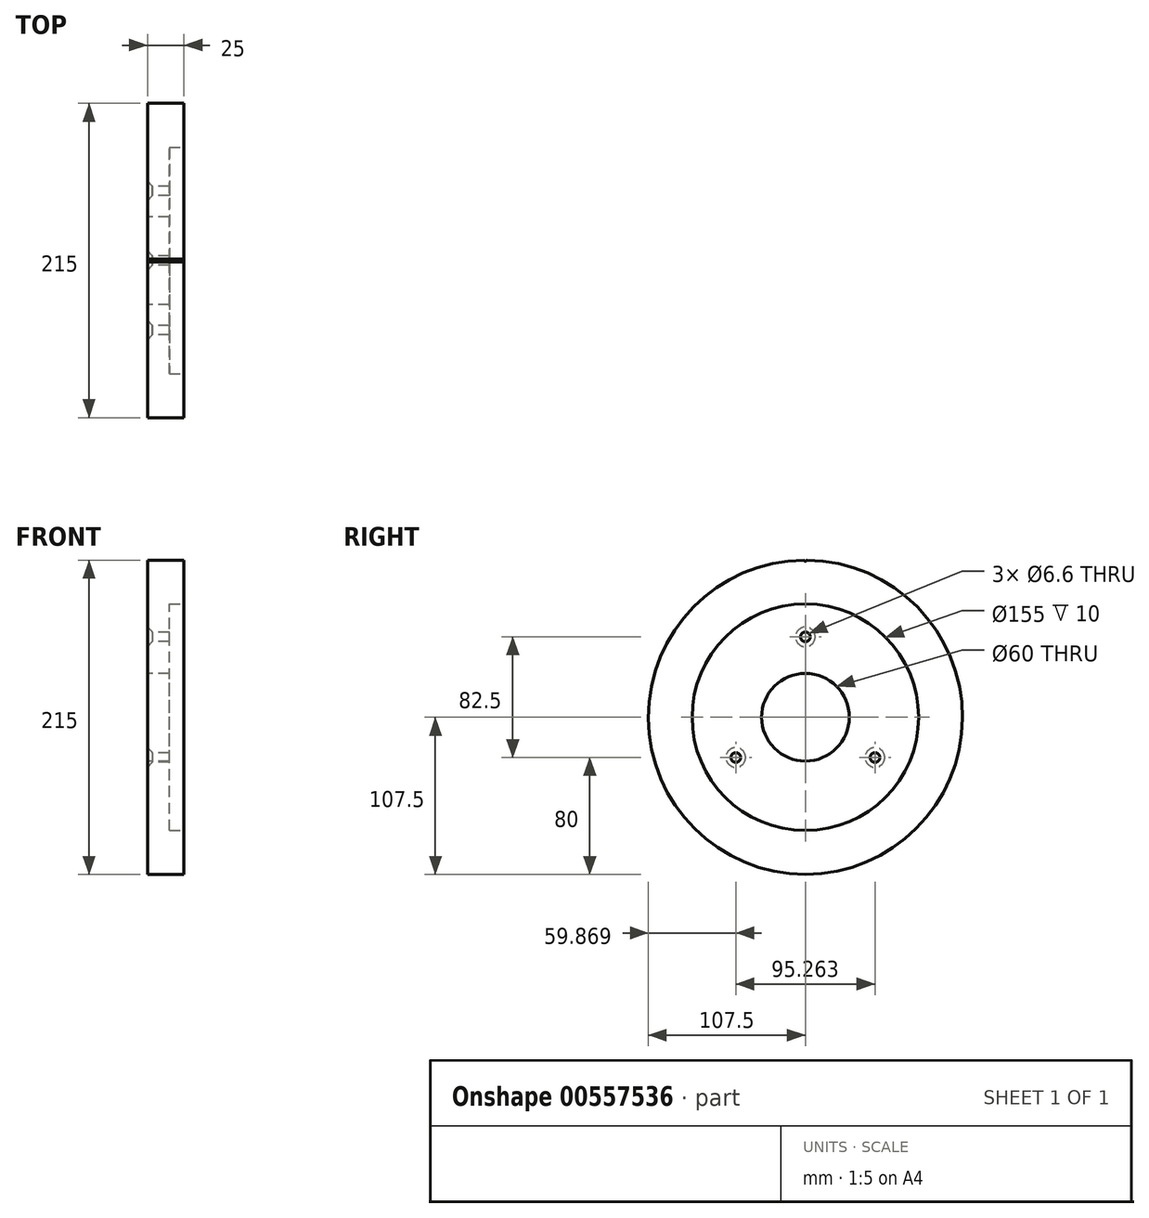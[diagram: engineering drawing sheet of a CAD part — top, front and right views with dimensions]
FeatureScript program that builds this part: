
annotation { "Feature Type Name" : "Feature", "Feature Type Description" : "" }
export const myFeature = defineFeature(function(context is Context, id is Id, definition is map)
    precondition{}
    {
        {
            var Q0;
            Q0=qCreatedBy(makeId("Right.planeOp"),FACE);
            var sketch = newSketch(context, id + "F0", { "sketchPlane" : qUnion([Q0])});
            skCircle(sketch, "E0", {"center": v(0, 0) * mm, "radius": 107.5 * mm});
            skSolve(sketch);
        }
        {
            var Q0;
            Q0 = qSketchRegion(id + "F0", true);
            extrude(context, id + "F1", {"entities" : qUnion([Q0]), "depth" : 25 * mm, "offsetDistance" : 25 * mm});
        }
        {
            var Q0;
            Q0=makeQuery(id+"F1.opExtrude","CAP_FACE",FACE,{"disambiguationData":[OSD([sQuery(id+"F0.wireOp",EDGE,"E0")])],"isStart":false});
            var sketch = newSketch(context, id + "F2", { "sketchPlane" : qUnion([Q0])});
            skCircle(sketch, "E1", {"center": v(0, 0) * mm, "radius": 77.5 * mm});
            skSolve(sketch);
        }
        {
            var Q0;
            Q0 = qSketchRegion(id + "F2", true);
            extrude(context, id + "F3", {"entities" : qUnion([Q0]), "operationType" : NewBodyOperationType.REMOVE, "oppositeDirection" : true, "depth" : 10 * mm, "offsetDistance" : 25 * mm});
        }
        {
            var Q0;
            Q0=makeQuery(id+"F1.opExtrude","CAP_FACE",FACE,{"disambiguationData":[OSD([sQuery(id+"F0.wireOp",EDGE,"E0")])],"isStart":true});
            var sketch = newSketch(context, id + "F4", { "sketchPlane" : qUnion([Q0])});
            skPoint(sketch, "E2", {"position": v(0, 55) * mm});
            skPoint(sketch, "E3.1.0", {"position": v(-47.63, -27.5) * mm});
            skPoint(sketch, "E3.2.0", {"position": v(47.63, -27.5) * mm});
            skPoint(sketch, "E3.center", {"position": v(0, 0) * mm});
            skSolve(sketch);
        }
        {
            var Q0;
            Q0=sQuery(id+"F4.wireOp",VERTEX,"E2");
            var Q1;
            Q1=sQuery(id+"F4.wireOp",VERTEX,"E3.2.0");
            var Q2;
            Q2=sQuery(id+"F4.wireOp",VERTEX,"E3.1.0");
            var Q3;
            Q3=makeQuery(id+"F1.opExtrude","SWEPT_BODY",BODY,{"disambiguationData":[OSD([sQuery(id+"F0.wireOp",EDGE,"E0")])]});
            hole(context, id + "F5", {"style" : HoleStyle.C_SINK, "endStyle" : HoleEndStyle.THROUGH, "standardTappedOrClearance" : lookupTablePath({ "standard" : "ISO", "fit" : "Normal", "size" : "M6", "type" : "Clearance" }), "standardBlindInLast" : lookupTablePath({ "fit" : "Standard", "standard" : "ISO", "size" : "M6", "type" : "Clearance" }), "holeDiameter" : 6.6 * mm, "cSinkDiameter" : 13.44 * mm, "cSinkAngle" : 90 * degree, "isTappedThrough" : true, "tappedDepth" : 12 * mm, "tapClearance" : 3, "locations" : qUnion([Q0, Q1, Q2]), "scope" : qUnion([Q3])});
        }
        {
            var Q0;
            Q0=makeQuery(id+"F1.opExtrude","CAP_FACE",FACE,{"disambiguationData":[OSD([sQuery(id+"F0.wireOp",EDGE,"E0")])],"isStart":true});
            var sketch = newSketch(context, id + "F6", { "sketchPlane" : qUnion([Q0])});
            skCircle(sketch, "E4", {"center": v(0, 0) * mm, "radius": 30 * mm});
            skSolve(sketch);
        }
        {
            var Q0;
            Q0 = qSketchRegion(id + "F6", true);
            extrude(context, id + "F7", {"entities" : qUnion([Q0]), "operationType" : NewBodyOperationType.REMOVE, "oppositeDirection" : true, "depth" : 25 * mm, "offsetDistance" : 25 * mm});
        }
        {
            var Q0;
            Q0=makeQuery(id+"F1.opExtrude","CAP_FACE",FACE,{"disambiguationData":[OSD([sQuery(id+"F0.wireOp",EDGE,"E0")])],"isStart":true});
            var sketch = newSketch(context, id + "F8", { "sketchPlane" : qUnion([Q0])});
            skCircle(sketch, "E5", {"center": v(0, 0) * mm, "radius": 107.85 * mm});
            skArc(sketch, "E6", {"start": v(-1, 107.84) * mm, "mid": v(0, 106.78) * mm, "end": v(1, 107.84) * mm});
            skSolve(sketch);
        }
        {
            var Q0;
            {var subQ0=sQuery(id+"F8.wireOp",EDGE,"E6");var subQ1=makeQuery(id+"F1.opExtrude","CAP_EDGE",EDGE,{"disambiguationData":[OSD([sQuery(id+"F0.wireOp",EDGE,"E0")])],"isStart":true});var subQ2=makeQuery(id+"F8.imprint","INTERSECT",VERTEX,{"disambiguationData":[OD(0.0)],"derivedFrom":[subQ1,subQ0]});Q0=makeQuery(id+"F8.imprint","IMPRINT",FACE,{"disambiguationData":[TD([[makeQuery(id+"F8.imprint","IMPRINT",EDGE,{"disambiguationData":[TD([[subQ2,-1.0]])],"derivedFrom":subQ0}),1.0]])]});}
            extrude(context, id + "F9", {"entities" : qUnion([Q0]), "operationType" : NewBodyOperationType.REMOVE, "oppositeDirection" : true, "depth" : 25 * mm, "offsetDistance" : 25 * mm});
        }
    });
